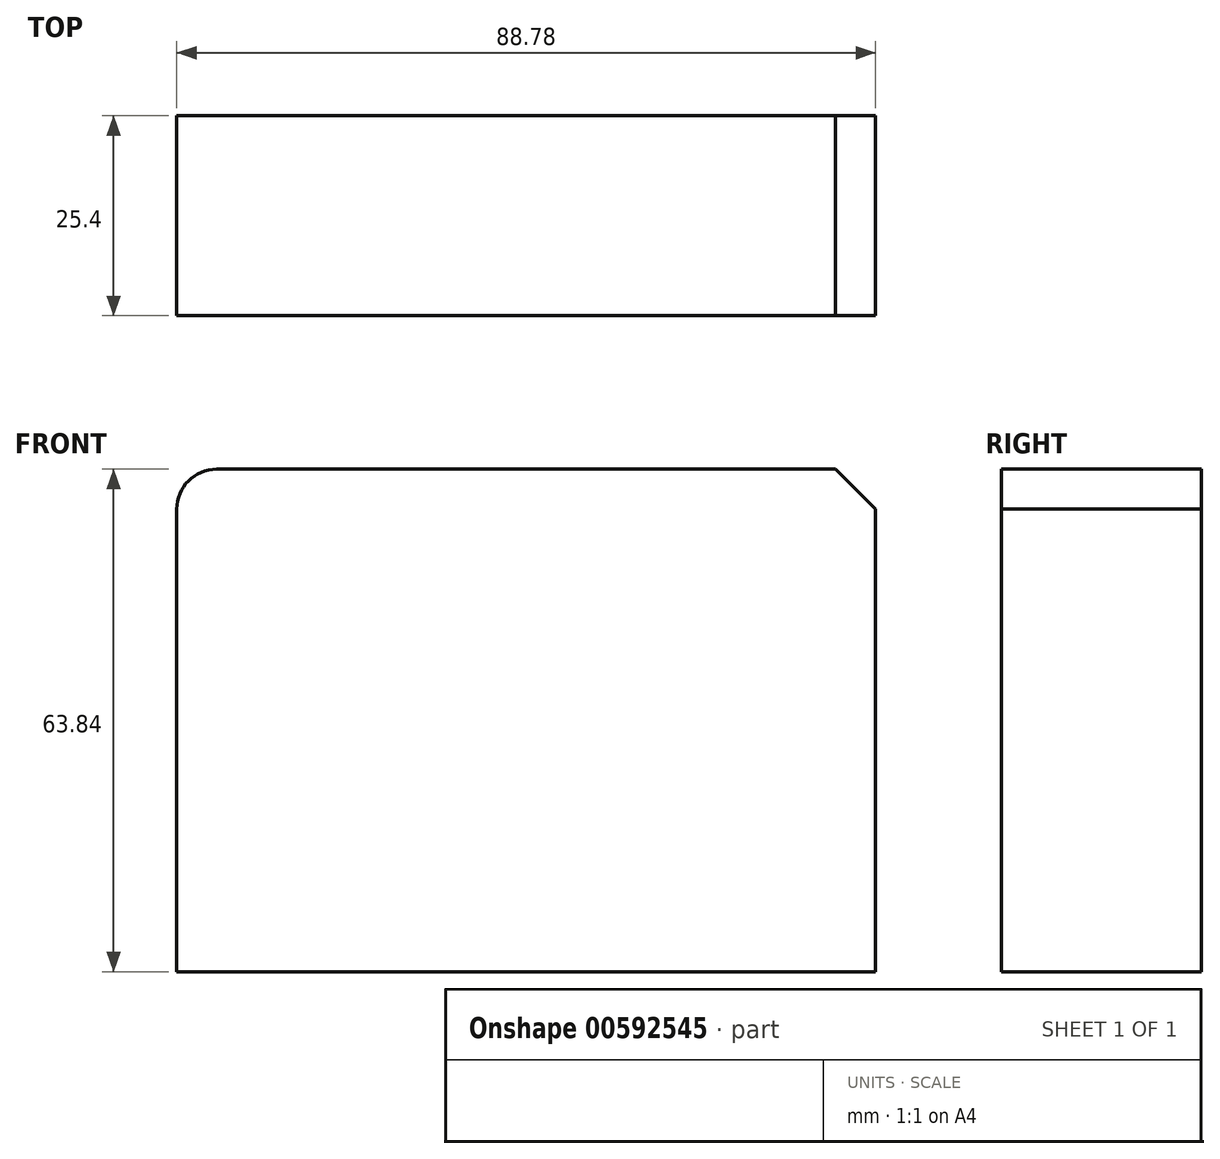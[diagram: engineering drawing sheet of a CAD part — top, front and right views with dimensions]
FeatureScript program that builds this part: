
annotation { "Feature Type Name" : "Feature", "Feature Type Description" : "" }
export const myFeature = defineFeature(function(context is Context, id is Id, definition is map)
    precondition{}
    {
        {
            var Q0;
            Q0=qCreatedBy(makeId("Front.planeOp"),FACE);
            var sketch = newSketch(context, id + "F0", { "sketchPlane" : qUnion([Q0])});
            skLineSegment(sketch, "E0.bottom", {"start": v(44.39, -31.92) * mm, "end": v(-44.39, -31.92) * mm});
            skLineSegment(sketch, "E0.top", {"start": v(44.39, 31.92) * mm, "end": v(-44.39, 31.92) * mm});
            skLineSegment(sketch, "E0.left", {"start": v(44.39, -31.92) * mm, "end": v(44.39, 31.92) * mm});
            skLineSegment(sketch, "E0.right", {"start": v(-44.39, -31.92) * mm, "end": v(-44.39, 31.92) * mm});
            skPoint(sketch, "E0.middle", {"position": v(0, 0) * mm});
            skSolve(sketch);
        }
        {
            var Q0;
            Q0 = qSketchRegion(id + "F0", true);
            extrude(context, id + "F1", {"entities" : qUnion([Q0]), "depth" : 25.4 * mm, "offsetDistance" : 25.4 * mm});
        }
        {
            var Q0;
            Q0=makeQuery(id+"F1.opExtrude","SWEPT_EDGE",EDGE,{"disambiguationData":[OSD([sQuery(id+"F0.wireOp",EDGE,"E0.top"),sQuery(id+"F0.wireOp",EDGE,"E0.right")])]});
            fillet(context, id + "F2", {"entities" : qUnion([Q0]), "radius" : 5.08 * mm, "tangentPropagation" : true, "allowEdgeOverflow" : false});
        }
        {
            var Q0;
            Q0=makeQuery(id+"F1.opExtrude","SWEPT_EDGE",EDGE,{"disambiguationData":[OSD([sQuery(id+"F0.wireOp",EDGE,"E0.top"),sQuery(id+"F0.wireOp",EDGE,"E0.left")])]});
            chamfer(context, id + "F3", {"entities" : qUnion([Q0]), "width" : 5.08 * mm, "tangentPropagation" : true});
        }
    });
